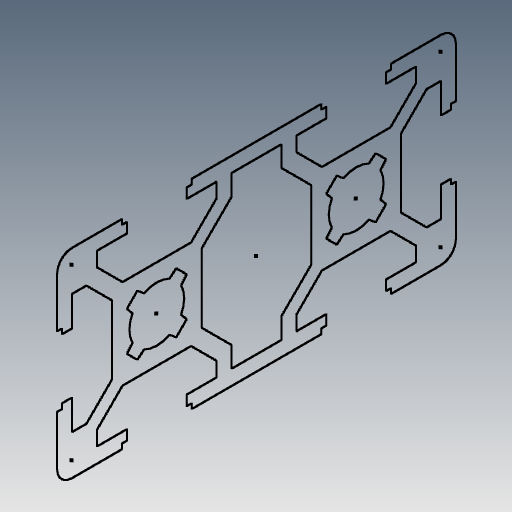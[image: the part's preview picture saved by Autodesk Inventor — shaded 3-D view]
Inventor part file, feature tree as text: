
AUTODESK INVENTOR PART (.ipt)
format: ipt  version: 2018.2 (Build 222227000, 227)  size: 121,344 bytes
history: native  units: mm
features: other x1, sketch x1
ambient origin geometry x8: Origin, YZ Plane, XZ Plane, XY Plane, X Axis, Y Axis, Z Axis, Center Point
feature tree (2):
  other  "STREBENPROFIL_20X40.ipt"
  sketch  "Skizze2"  dims[d0=10.0mm]
